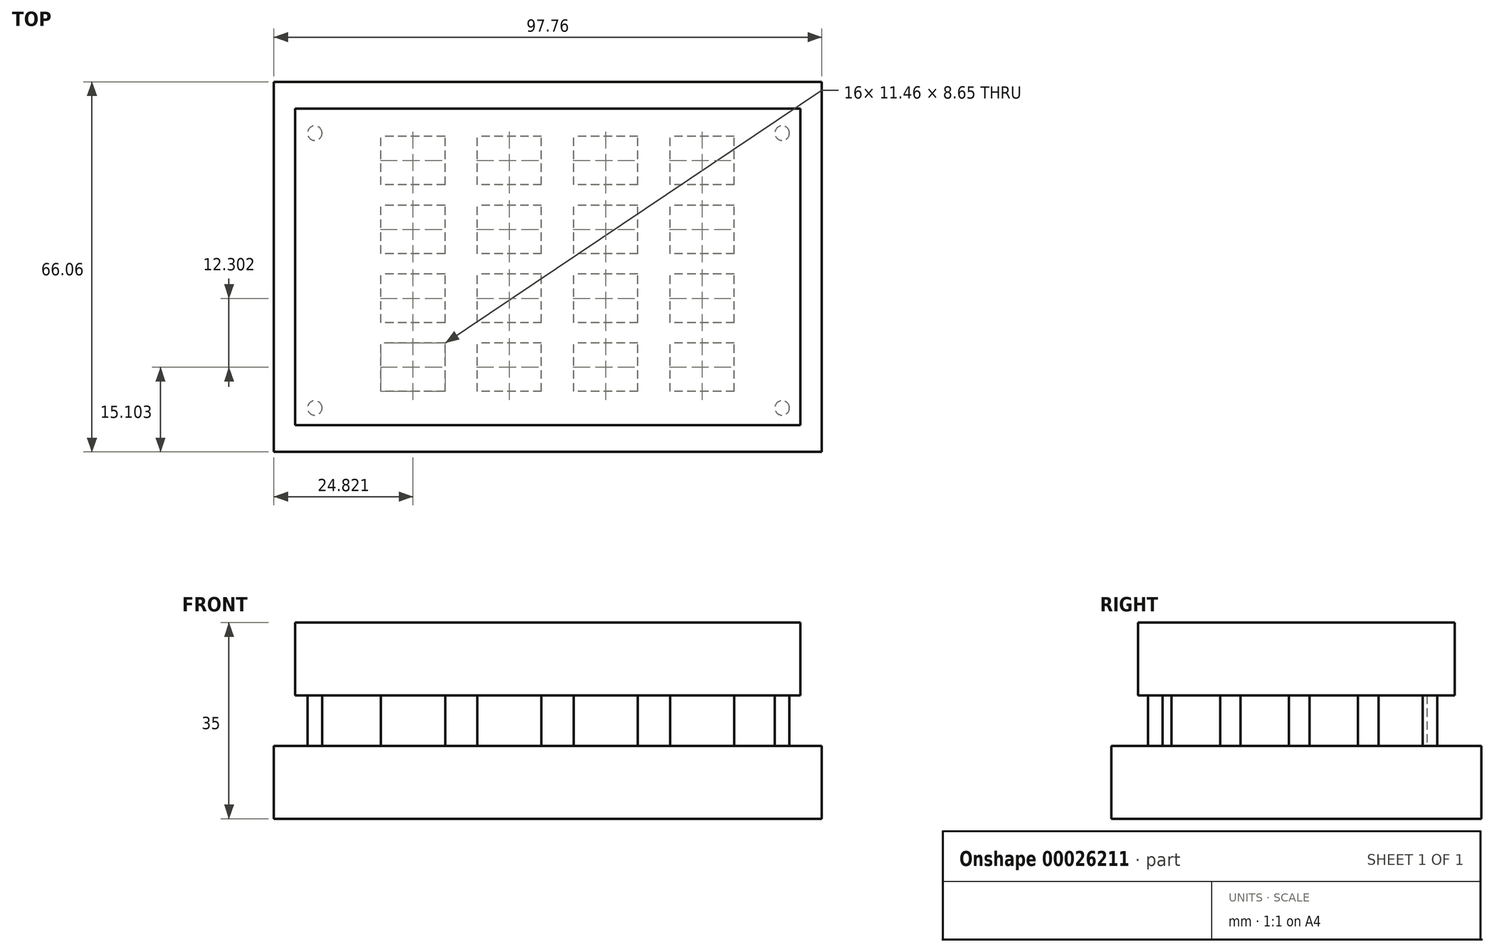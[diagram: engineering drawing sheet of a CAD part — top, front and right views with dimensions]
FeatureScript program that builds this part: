
annotation { "Feature Type Name" : "Feature", "Feature Type Description" : "" }
export const myFeature = defineFeature(function(context is Context, id is Id, definition is map)
    precondition{}
    {
        {
            var Q0;
            Q0=qCreatedBy(makeId("Top.planeOp"),FACE);
            var sketch = newSketch(context, id + "F0", { "sketchPlane" : qUnion([Q0])});
            skLineSegment(sketch, "E0.rect.bottom", {"start": v(-48.88, -33.03) * mm, "end": v(48.88, -33.03) * mm});
            skLineSegment(sketch, "E0.rect.top", {"start": v(-48.88, 33.03) * mm, "end": v(48.88, 33.03) * mm});
            skLineSegment(sketch, "E0.rect.left", {"start": v(-48.88, -33.03) * mm, "end": v(-48.88, 33.03) * mm});
            skLineSegment(sketch, "E0.rect.right", {"start": v(48.88, -33.03) * mm, "end": v(48.88, 33.03) * mm});
            skPoint(sketch, "E0.rect.middle", {"position": v(0, 0) * mm});
            skSolve(sketch);
        }
        {
            var Q0;
            Q0 = qSketchRegion(id + "F0", true);
            extrude(context, id + "F1", {"entities" : qUnion([Q0]), "depth" : 13 * mm});
        }
        {
            var Q0;
            Q0=makeQuery(id+"F1.opExtrude","CAP_FACE",FACE,{"disambiguationData":[OSD([sQuery(id+"F0.wireOp",EDGE,"E0.rect.bottom"),sQuery(id+"F0.wireOp",EDGE,"E0.rect.top"),sQuery(id+"F0.wireOp",EDGE,"E0.rect.left"),sQuery(id+"F0.wireOp",EDGE,"E0.rect.right")])],"isStart":false});
            var sketch = newSketch(context, id + "F2", { "sketchPlane" : qUnion([Q0])});
            skLineSegment(sketch, "E1.rect.bottom", {"start": v(-18.33, 14.66) * mm, "end": v(-29.79, 14.66) * mm});
            skLineSegment(sketch, "E1.rect.top", {"start": v(-18.33, 23.3) * mm, "end": v(-29.79, 23.3) * mm});
            skLineSegment(sketch, "E1.rect.left", {"start": v(-18.33, 14.66) * mm, "end": v(-18.33, 23.3) * mm});
            skLineSegment(sketch, "E1.rect.right", {"start": v(-29.79, 14.66) * mm, "end": v(-29.79, 23.3) * mm});
            skPoint(sketch, "E1.rect.middle", {"position": v(-24.06, 18.98) * mm});
            skLineSegment(sketch, "E2.0.1.0", {"start": v(-29.79, 2.35) * mm, "end": v(-29.79, 11) * mm});
            skLineSegment(sketch, "E2.0.1.1", {"start": v(-18.33, 2.35) * mm, "end": v(-18.33, 11) * mm});
            skLineSegment(sketch, "E2.0.1.2", {"start": v(-18.33, 11) * mm, "end": v(-29.79, 11) * mm});
            skLineSegment(sketch, "E2.0.1.3", {"start": v(-18.33, 2.35) * mm, "end": v(-29.79, 2.35) * mm});
            skPoint(sketch, "E2.0.1.4", {"position": v(-24.06, 6.68) * mm});
            skLineSegment(sketch, "E2.0.2.0", {"start": v(-29.79, -9.95) * mm, "end": v(-29.79, -1.3) * mm});
            skLineSegment(sketch, "E2.0.2.1", {"start": v(-18.33, -9.95) * mm, "end": v(-18.33, -1.3) * mm});
            skLineSegment(sketch, "E2.0.2.2", {"start": v(-18.33, -1.3) * mm, "end": v(-29.79, -1.3) * mm});
            skLineSegment(sketch, "E2.0.2.3", {"start": v(-18.33, -9.95) * mm, "end": v(-29.79, -9.95) * mm});
            skPoint(sketch, "E2.0.2.4", {"position": v(-24.06, -5.62) * mm});
            skLineSegment(sketch, "E2.0.3.0", {"start": v(-29.79, -22.25) * mm, "end": v(-29.79, -13.6) * mm});
            skLineSegment(sketch, "E2.0.3.1", {"start": v(-18.33, -22.25) * mm, "end": v(-18.33, -13.6) * mm});
            skLineSegment(sketch, "E2.0.3.2", {"start": v(-18.33, -13.6) * mm, "end": v(-29.79, -13.6) * mm});
            skLineSegment(sketch, "E2.0.3.3", {"start": v(-18.33, -22.25) * mm, "end": v(-29.79, -22.25) * mm});
            skPoint(sketch, "E2.0.3.4", {"position": v(-24.06, -17.93) * mm});
            skLineSegment(sketch, "E2.1.0.0", {"start": v(-12.59, 14.66) * mm, "end": v(-12.59, 23.3) * mm});
            skLineSegment(sketch, "E2.1.0.1", {"start": v(-1.12, 14.66) * mm, "end": v(-1.12, 23.3) * mm});
            skLineSegment(sketch, "E2.1.0.2", {"start": v(-1.12, 23.3) * mm, "end": v(-12.59, 23.3) * mm});
            skLineSegment(sketch, "E2.1.0.3", {"start": v(-1.12, 14.66) * mm, "end": v(-12.59, 14.66) * mm});
            skPoint(sketch, "E2.1.0.4", {"position": v(-6.85, 18.98) * mm});
            skLineSegment(sketch, "E2.1.1.0", {"start": v(-12.59, 2.35) * mm, "end": v(-12.59, 11) * mm});
            skLineSegment(sketch, "E2.1.1.1", {"start": v(-1.12, 2.35) * mm, "end": v(-1.12, 11) * mm});
            skLineSegment(sketch, "E2.1.1.2", {"start": v(-1.12, 11) * mm, "end": v(-12.59, 11) * mm});
            skLineSegment(sketch, "E2.1.1.3", {"start": v(-1.12, 2.35) * mm, "end": v(-12.59, 2.35) * mm});
            skPoint(sketch, "E2.1.1.4", {"position": v(-6.85, 6.68) * mm});
            skLineSegment(sketch, "E2.1.2.0", {"start": v(-12.59, -9.95) * mm, "end": v(-12.59, -1.3) * mm});
            skLineSegment(sketch, "E2.1.2.1", {"start": v(-1.12, -9.95) * mm, "end": v(-1.12, -1.3) * mm});
            skLineSegment(sketch, "E2.1.2.2", {"start": v(-1.12, -1.3) * mm, "end": v(-12.59, -1.3) * mm});
            skLineSegment(sketch, "E2.1.2.3", {"start": v(-1.12, -9.95) * mm, "end": v(-12.59, -9.95) * mm});
            skPoint(sketch, "E2.1.2.4", {"position": v(-6.85, -5.62) * mm});
            skLineSegment(sketch, "E2.1.3.0", {"start": v(-12.59, -22.25) * mm, "end": v(-12.59, -13.6) * mm});
            skLineSegment(sketch, "E2.1.3.1", {"start": v(-1.12, -22.25) * mm, "end": v(-1.12, -13.6) * mm});
            skLineSegment(sketch, "E2.1.3.2", {"start": v(-1.12, -13.6) * mm, "end": v(-12.59, -13.6) * mm});
            skLineSegment(sketch, "E2.1.3.3", {"start": v(-1.12, -22.25) * mm, "end": v(-12.59, -22.25) * mm});
            skPoint(sketch, "E2.1.3.4", {"position": v(-6.85, -17.93) * mm});
            skLineSegment(sketch, "E2.2.0.0", {"start": v(4.62, 14.66) * mm, "end": v(4.62, 23.3) * mm});
            skLineSegment(sketch, "E2.2.0.1", {"start": v(16.08, 14.66) * mm, "end": v(16.08, 23.3) * mm});
            skLineSegment(sketch, "E2.2.0.2", {"start": v(16.08, 23.3) * mm, "end": v(4.62, 23.3) * mm});
            skLineSegment(sketch, "E2.2.0.3", {"start": v(16.08, 14.66) * mm, "end": v(4.62, 14.66) * mm});
            skPoint(sketch, "E2.2.0.4", {"position": v(10.35, 18.98) * mm});
            skLineSegment(sketch, "E2.2.1.0", {"start": v(4.62, 2.35) * mm, "end": v(4.62, 11) * mm});
            skLineSegment(sketch, "E2.2.1.1", {"start": v(16.08, 2.35) * mm, "end": v(16.08, 11) * mm});
            skLineSegment(sketch, "E2.2.1.2", {"start": v(16.08, 11) * mm, "end": v(4.62, 11) * mm});
            skLineSegment(sketch, "E2.2.1.3", {"start": v(16.08, 2.35) * mm, "end": v(4.62, 2.35) * mm});
            skPoint(sketch, "E2.2.1.4", {"position": v(10.35, 6.68) * mm});
            skLineSegment(sketch, "E2.2.2.0", {"start": v(4.62, -9.95) * mm, "end": v(4.62, -1.3) * mm});
            skLineSegment(sketch, "E2.2.2.1", {"start": v(16.08, -9.95) * mm, "end": v(16.08, -1.3) * mm});
            skLineSegment(sketch, "E2.2.2.2", {"start": v(16.08, -1.3) * mm, "end": v(4.62, -1.3) * mm});
            skLineSegment(sketch, "E2.2.2.3", {"start": v(16.08, -9.95) * mm, "end": v(4.62, -9.95) * mm});
            skPoint(sketch, "E2.2.2.4", {"position": v(10.35, -5.62) * mm});
            skLineSegment(sketch, "E2.2.3.0", {"start": v(4.62, -22.25) * mm, "end": v(4.62, -13.6) * mm});
            skLineSegment(sketch, "E2.2.3.1", {"start": v(16.08, -22.25) * mm, "end": v(16.08, -13.6) * mm});
            skLineSegment(sketch, "E2.2.3.2", {"start": v(16.08, -13.6) * mm, "end": v(4.62, -13.6) * mm});
            skLineSegment(sketch, "E2.2.3.3", {"start": v(16.08, -22.25) * mm, "end": v(4.62, -22.25) * mm});
            skPoint(sketch, "E2.2.3.4", {"position": v(10.35, -17.93) * mm});
            skLineSegment(sketch, "E2.3.0.0", {"start": v(21.82, 14.66) * mm, "end": v(21.82, 23.3) * mm});
            skLineSegment(sketch, "E2.3.0.1", {"start": v(33.28, 14.66) * mm, "end": v(33.28, 23.3) * mm});
            skLineSegment(sketch, "E2.3.0.2", {"start": v(33.28, 23.3) * mm, "end": v(21.82, 23.3) * mm});
            skLineSegment(sketch, "E2.3.0.3", {"start": v(33.28, 14.66) * mm, "end": v(21.82, 14.66) * mm});
            skPoint(sketch, "E2.3.0.4", {"position": v(27.55, 18.98) * mm});
            skLineSegment(sketch, "E2.3.1.0", {"start": v(21.82, 2.35) * mm, "end": v(21.82, 11) * mm});
            skLineSegment(sketch, "E2.3.1.1", {"start": v(33.28, 2.35) * mm, "end": v(33.28, 11) * mm});
            skLineSegment(sketch, "E2.3.1.2", {"start": v(33.28, 11) * mm, "end": v(21.82, 11) * mm});
            skLineSegment(sketch, "E2.3.1.3", {"start": v(33.28, 2.35) * mm, "end": v(21.82, 2.35) * mm});
            skPoint(sketch, "E2.3.1.4", {"position": v(27.55, 6.68) * mm});
            skLineSegment(sketch, "E2.3.2.0", {"start": v(21.82, -9.95) * mm, "end": v(21.82, -1.3) * mm});
            skLineSegment(sketch, "E2.3.2.1", {"start": v(33.28, -9.95) * mm, "end": v(33.28, -1.3) * mm});
            skLineSegment(sketch, "E2.3.2.2", {"start": v(33.28, -1.3) * mm, "end": v(21.82, -1.3) * mm});
            skLineSegment(sketch, "E2.3.2.3", {"start": v(33.28, -9.95) * mm, "end": v(21.82, -9.95) * mm});
            skPoint(sketch, "E2.3.2.4", {"position": v(27.55, -5.62) * mm});
            skLineSegment(sketch, "E2.3.3.0", {"start": v(21.82, -22.25) * mm, "end": v(21.82, -13.6) * mm});
            skLineSegment(sketch, "E2.3.3.1", {"start": v(33.28, -22.25) * mm, "end": v(33.28, -13.6) * mm});
            skLineSegment(sketch, "E2.3.3.2", {"start": v(33.28, -13.6) * mm, "end": v(21.82, -13.6) * mm});
            skLineSegment(sketch, "E2.3.3.3", {"start": v(33.28, -22.25) * mm, "end": v(21.82, -22.25) * mm});
            skPoint(sketch, "E2.3.3.4", {"position": v(27.55, -17.93) * mm});
            skLineSegment(sketch, "E2.direction1", {"start": v(-29.79, 14.66) * mm, "end": v(-12.59, 14.66) * mm, "construction": true});
            skLineSegment(sketch, "E2.direction2", {"start": v(-29.79, 14.66) * mm, "end": v(-29.79, 2.35) * mm, "construction": true});
            skSolve(sketch);
        }
        {
            var Q0;
            Q0=makeQuery(id+"F2.imprint","IMPRINT",FACE,{"disambiguationData":[TD([[makeQuery(id+"F2.imprint","IMPRINT",EDGE,{"derivedFrom":sQuery(id+"F2.wireOp",EDGE,"E2.3.3.0")}),-1.0]])]});
            var Q1;
            Q1=makeQuery(id+"F2.imprint","IMPRINT",FACE,{"disambiguationData":[TD([[makeQuery(id+"F2.imprint","IMPRINT",EDGE,{"derivedFrom":sQuery(id+"F2.wireOp",EDGE,"E2.3.1.0")}),-1.0]])]});
            var Q2;
            Q2=makeQuery(id+"F2.imprint","IMPRINT",FACE,{"disambiguationData":[TD([[makeQuery(id+"F2.imprint","IMPRINT",EDGE,{"derivedFrom":sQuery(id+"F2.wireOp",EDGE,"E2.3.2.0")}),-1.0]])]});
            var Q3;
            Q3=makeQuery(id+"F2.imprint","IMPRINT",FACE,{"disambiguationData":[TD([[makeQuery(id+"F2.imprint","IMPRINT",EDGE,{"derivedFrom":sQuery(id+"F2.wireOp",EDGE,"E1.rect.bottom")}),-1.0]])]});
            var Q4;
            Q4=makeQuery(id+"F2.imprint","IMPRINT",FACE,{"disambiguationData":[TD([[makeQuery(id+"F2.imprint","IMPRINT",EDGE,{"derivedFrom":sQuery(id+"F2.wireOp",EDGE,"E2.0.1.0")}),-1.0]])]});
            var Q5;
            Q5=makeQuery(id+"F2.imprint","IMPRINT",FACE,{"disambiguationData":[TD([[makeQuery(id+"F2.imprint","IMPRINT",EDGE,{"derivedFrom":sQuery(id+"F2.wireOp",EDGE,"E2.0.2.0")}),-1.0]])]});
            var Q6;
            Q6=makeQuery(id+"F2.imprint","IMPRINT",FACE,{"disambiguationData":[TD([[makeQuery(id+"F2.imprint","IMPRINT",EDGE,{"derivedFrom":sQuery(id+"F2.wireOp",EDGE,"E2.0.3.0")}),-1.0]])]});
            var Q7;
            Q7=makeQuery(id+"F2.imprint","IMPRINT",FACE,{"disambiguationData":[TD([[makeQuery(id+"F2.imprint","IMPRINT",EDGE,{"derivedFrom":sQuery(id+"F2.wireOp",EDGE,"E2.1.0.0")}),-1.0]])]});
            var Q8;
            Q8=makeQuery(id+"F2.imprint","IMPRINT",FACE,{"disambiguationData":[TD([[makeQuery(id+"F2.imprint","IMPRINT",EDGE,{"derivedFrom":sQuery(id+"F2.wireOp",EDGE,"E2.1.1.0")}),-1.0]])]});
            var Q9;
            Q9=makeQuery(id+"F2.imprint","IMPRINT",FACE,{"disambiguationData":[TD([[makeQuery(id+"F2.imprint","IMPRINT",EDGE,{"derivedFrom":sQuery(id+"F2.wireOp",EDGE,"E2.1.2.0")}),-1.0]])]});
            var Q10;
            Q10=makeQuery(id+"F2.imprint","IMPRINT",FACE,{"disambiguationData":[TD([[makeQuery(id+"F2.imprint","IMPRINT",EDGE,{"derivedFrom":sQuery(id+"F2.wireOp",EDGE,"E2.1.3.0")}),-1.0]])]});
            var Q11;
            Q11=makeQuery(id+"F2.imprint","IMPRINT",FACE,{"disambiguationData":[TD([[makeQuery(id+"F2.imprint","IMPRINT",EDGE,{"derivedFrom":sQuery(id+"F2.wireOp",EDGE,"E2.2.0.0")}),-1.0]])]});
            var Q12;
            Q12=makeQuery(id+"F2.imprint","IMPRINT",FACE,{"disambiguationData":[TD([[makeQuery(id+"F2.imprint","IMPRINT",EDGE,{"derivedFrom":sQuery(id+"F2.wireOp",EDGE,"E2.2.1.0")}),-1.0]])]});
            var Q13;
            Q13=makeQuery(id+"F2.imprint","IMPRINT",FACE,{"disambiguationData":[TD([[makeQuery(id+"F2.imprint","IMPRINT",EDGE,{"derivedFrom":sQuery(id+"F2.wireOp",EDGE,"E2.2.2.0")}),-1.0]])]});
            var Q14;
            Q14=makeQuery(id+"F2.imprint","IMPRINT",FACE,{"disambiguationData":[TD([[makeQuery(id+"F2.imprint","IMPRINT",EDGE,{"derivedFrom":sQuery(id+"F2.wireOp",EDGE,"E2.2.3.0")}),-1.0]])]});
            var Q15;
            Q15=makeQuery(id+"F2.imprint","IMPRINT",FACE,{"disambiguationData":[TD([[makeQuery(id+"F2.imprint","IMPRINT",EDGE,{"derivedFrom":sQuery(id+"F2.wireOp",EDGE,"E2.3.0.0")}),-1.0]])]});
            extrude(context, id + "F3", {"entities" : qUnion([Q0, Q1, Q2, Q3, Q4, Q5, Q6, Q7, Q8, Q9, Q10, Q11, Q12, Q13, Q14, Q15]), "depth" : 9 * mm});
        }
        {
            var Q0;
            Q0=makeQuery(id+"F3.opExtrude","CAP_FACE",FACE,{"disambiguationData":[OSD([sQuery(id+"F2.wireOp",EDGE,"E2.0.2.0"),sQuery(id+"F2.wireOp",EDGE,"E2.0.2.1"),sQuery(id+"F2.wireOp",EDGE,"E2.0.2.2"),sQuery(id+"F2.wireOp",EDGE,"E2.0.2.3")])],"isStart":false});
            var sketch = newSketch(context, id + "F4", { "sketchPlane" : qUnion([Q0])});
            skLineSegment(sketch, "E3.rect.bottom", {"start": v(-45.1, 28.27) * mm, "end": v(45.1, 28.27) * mm});
            skLineSegment(sketch, "E3.rect.top", {"start": v(-45.1, -28.27) * mm, "end": v(45.1, -28.27) * mm});
            skLineSegment(sketch, "E3.rect.left", {"start": v(-45.1, 28.27) * mm, "end": v(-45.1, -28.27) * mm});
            skLineSegment(sketch, "E3.rect.right", {"start": v(45.1, 28.27) * mm, "end": v(45.1, -28.27) * mm});
            skPoint(sketch, "E3.rect.middle", {"position": v(0, 0) * mm});
            skSolve(sketch);
        }
        {
            var Q0;
            Q0 = qSketchRegion(id + "F4", true);
            extrude(context, id + "F5", {"entities" : qUnion([Q0]), "operationType" : NewBodyOperationType.ADD, "depth" : 13 * mm});
        }
        {
            var Q0;
            Q0=makeQuery(id+"F5.opExtrude","CAP_FACE",FACE,{"disambiguationData":[OSD([sQuery(id+"F4.wireOp",EDGE,"E3.rect.bottom"),sQuery(id+"F4.wireOp",EDGE,"E3.rect.top"),sQuery(id+"F4.wireOp",EDGE,"E3.rect.left"),sQuery(id+"F4.wireOp",EDGE,"E3.rect.right")])],"isStart":false});
            var sketch = newSketch(context, id + "F6", { "sketchPlane" : qUnion([Q0])});
            skCircle(sketch, "E4", {"center": v(-41.57, 23.87) * mm, "radius": 1.3 * mm});
            skCircle(sketch, "E5.0.1.1", {"center": v(-41.57, -25.19) * mm, "radius": 1.3 * mm});
            skCircle(sketch, "E5.1.0.1", {"center": v(41.83, 23.87) * mm, "radius": 1.3 * mm});
            skCircle(sketch, "E5.1.1.1", {"center": v(41.83, -25.19) * mm, "radius": 1.3 * mm});
            skLineSegment(sketch, "E5.direction1", {"start": v(-41.57, 23.87) * mm, "end": v(41.83, 23.87) * mm, "construction": true});
            skLineSegment(sketch, "E5.direction2", {"start": v(-41.57, 23.87) * mm, "end": v(-41.57, -25.19) * mm, "construction": true});
            skSolve(sketch);
        }
        {
            var Q0;
            Q0 = qSketchRegion(id + "F6", true);
            extrude(context, id + "F7", {"entities" : qUnion([Q0]), "operationType" : NewBodyOperationType.ADD, "oppositeDirection" : true, "depth" : 25 * mm});
        }
    });
